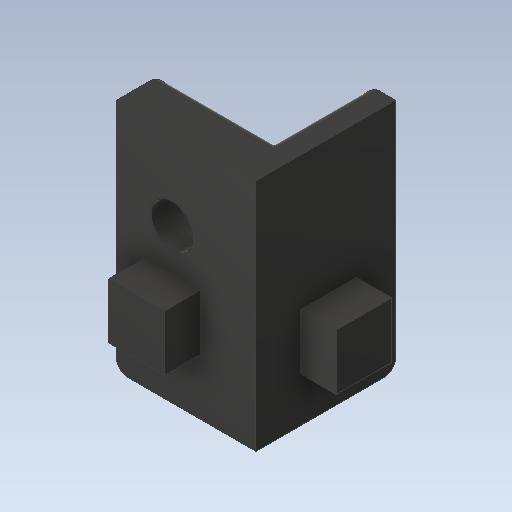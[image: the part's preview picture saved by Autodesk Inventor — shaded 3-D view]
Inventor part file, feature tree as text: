
AUTODESK INVENTOR PART (.ipt)
format: ipt  version: 2020 (Build 240168000, 168)  size: 179,712 bytes
history: native  units: in
note: dims shown in document units (in); Inventor stores cm internally (conversion verified against a paired STEP export)
features: sketch x13, other x3
ambient origin geometry x8: Origin, YZ Plane, XZ Plane, XY Plane, X Axis, Y Axis, Z Axis, Center Point
bodies: Solid1 (feature_tree)
feature tree (16):
  other  "frame-holder-v3.ipt"
  other  "Solid1::frame-holder-v3.ipt"
  other  "TaggingFeature1"
  sketch  "Sketch1"  dims[d0=0.3937in]
  sketch  "Sketch2"
  sketch  "Sketch3"
  sketch  "Sketch4"
  sketch  "Sketch6"
  sketch  "Sketch9"
  sketch  "Sketch12"
  sketch  "Sketch14"
  sketch  "Sketch15"
  sketch  "Sketch10"
  sketch  "Sketch7"
  sketch  "Sketch8"
  sketch  "Sketch5"
